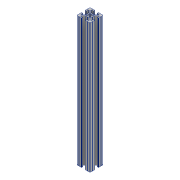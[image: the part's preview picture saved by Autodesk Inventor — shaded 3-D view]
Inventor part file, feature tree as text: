
AUTODESK INVENTOR PART (.ipt)
format: ipt  version: 2018.1 (Build 221171000, 171)  size: 204,800 bytes
history: native  units: mm
features: other x2, extrude x1
ambient origin geometry x8: Origin, YZ Plane, XZ Plane, XY Plane, X Axis, Y Axis, Z Axis, Center Point
bodies: Volumenkörper1 (feature_tree)
feature tree (3):
  other  "Vorlage_Aluprofile_30x30.ipt"
  extrude  "Extrusion1"  Depth=10.0mm
  other  "Profil_Skizze"
